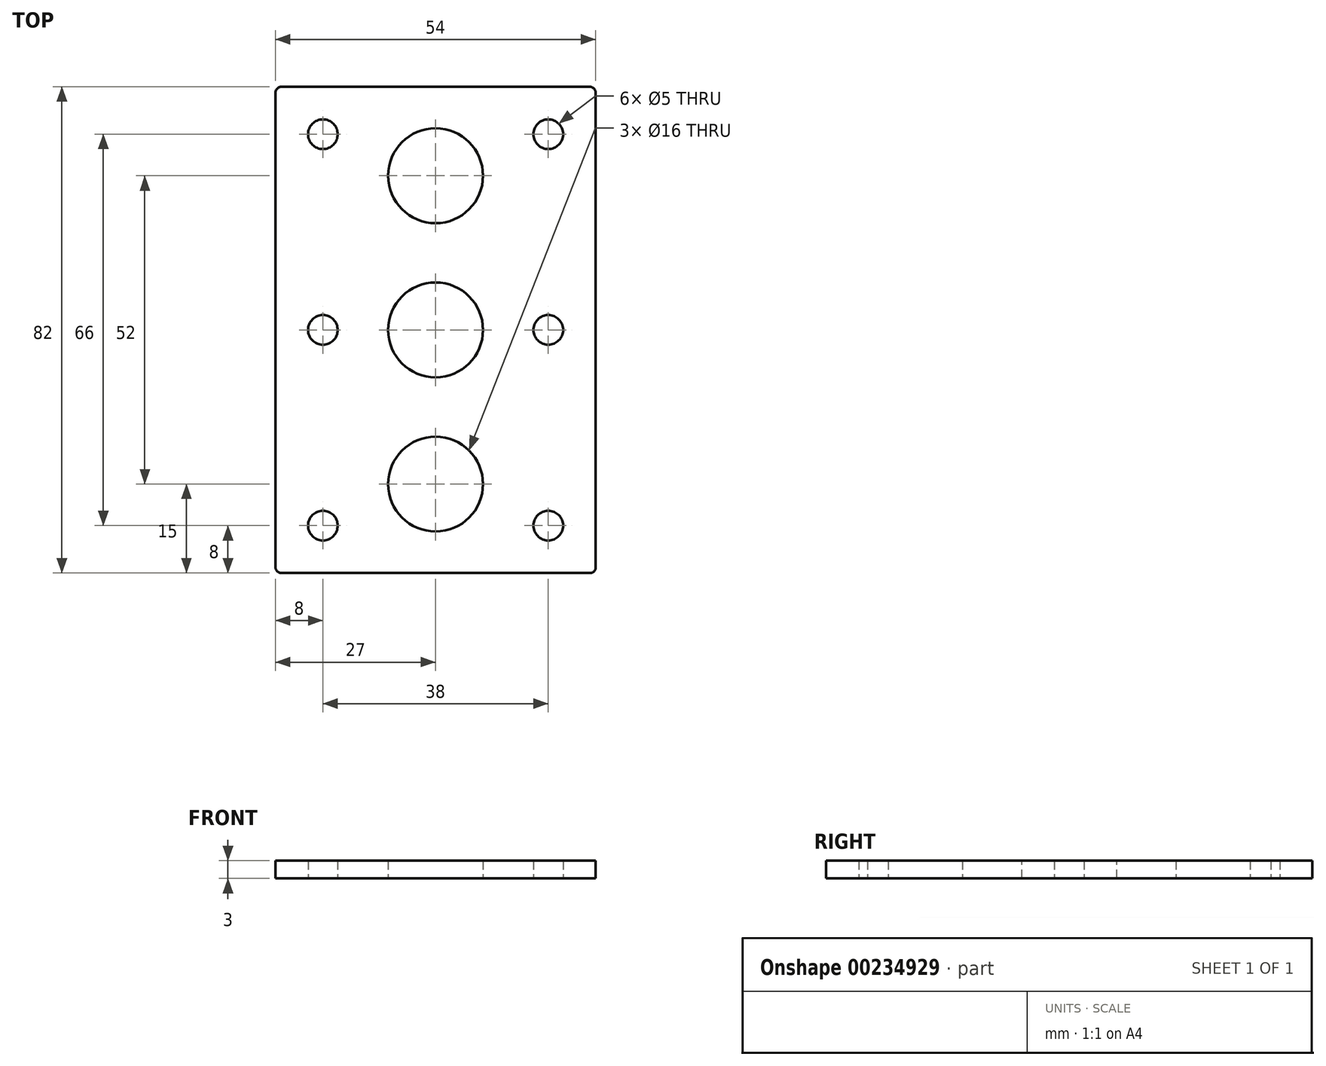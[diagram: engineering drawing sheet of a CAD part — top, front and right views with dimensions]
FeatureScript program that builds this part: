
annotation { "Feature Type Name" : "Feature", "Feature Type Description" : "" }
export const myFeature = defineFeature(function(context is Context, id is Id, definition is map)
    precondition{}
    {
        {
            var Q0;
            Q0=qCreatedBy(makeId("Top.planeOp"),FACE);
            var sketch = newSketch(context, id + "F0", { "sketchPlane" : qUnion([Q0])});
            skLineSegment(sketch, "E0.bottom", {"start": v(27, 41) * mm, "end": v(-27, 41) * mm});
            skLineSegment(sketch, "E0.top", {"start": v(27, -41) * mm, "end": v(-27, -41) * mm});
            skLineSegment(sketch, "E0.left", {"start": v(27, 41) * mm, "end": v(27, -41) * mm});
            skLineSegment(sketch, "E0.right", {"start": v(-27, 41) * mm, "end": v(-27, -41) * mm});
            skPoint(sketch, "E0.middle", {"position": v(0, 0) * mm});
            skLineSegment(sketch, "E1", {"start": v(0, -41) * mm, "end": v(0, 41) * mm, "construction": true});
            skCircle(sketch, "E2", {"center": v(0, -26) * mm, "radius": 8 * mm});
            skCircle(sketch, "E3", {"center": v(0, 26) * mm, "radius": 8 * mm});
            skLineSegment(sketch, "E4", {"start": v(-19, 41) * mm, "end": v(-19, -41) * mm, "construction": true});
            skLineSegment(sketch, "E5", {"start": v(0, 0) * mm, "end": v(-27, 0) * mm, "construction": true});
            skCircle(sketch, "E6", {"center": v(-19, 0) * mm, "radius": 2.5 * mm});
            skCircle(sketch, "E7", {"center": v(-19, -33) * mm, "radius": 2.5 * mm});
            skCircle(sketch, "E8", {"center": v(-19, 33) * mm, "radius": 2.5 * mm});
            skCircle(sketch, "E9.MirrorC", {"center": v(19, 33) * mm, "radius": 2.5 * mm});
            skCircle(sketch, "E10.MirrorC", {"center": v(19, 0) * mm, "radius": 2.5 * mm});
            skCircle(sketch, "E11.MirrorC", {"center": v(19, -33) * mm, "radius": 2.5 * mm});
            skSolve(sketch);
        }
        {
            var Q0;
            Q0 = qSketchRegion(id + "F0", true);
            extrude(context, id + "F1", {"entities" : qUnion([Q0]), "depth" : 5 * mm, "offsetDistance" : 25 * mm});
        }
        {
            var Q0;
            Q0=makeQuery(id+"F1.opExtrude","SWEPT_EDGE",EDGE,{"disambiguationData":[OSD([sQuery(id+"F0.wireOp",EDGE,"E0.top"),sQuery(id+"F0.wireOp",EDGE,"E0.left")])]});
            var Q1;
            Q1=makeQuery(id+"F1.opExtrude","SWEPT_EDGE",EDGE,{"disambiguationData":[OSD([sQuery(id+"F0.wireOp",EDGE,"E0.top"),sQuery(id+"F0.wireOp",EDGE,"E0.right")])]});
            var Q2;
            Q2=makeQuery(id+"F1.opExtrude","SWEPT_EDGE",EDGE,{"disambiguationData":[OSD([sQuery(id+"F0.wireOp",EDGE,"E0.bottom"),sQuery(id+"F0.wireOp",EDGE,"E0.right")])]});
            var Q3;
            Q3=makeQuery(id+"F1.opExtrude","SWEPT_EDGE",EDGE,{"disambiguationData":[OSD([sQuery(id+"F0.wireOp",EDGE,"E0.bottom"),sQuery(id+"F0.wireOp",EDGE,"E0.left")])]});
            fillet(context, id + "F2", {"entities" : qUnion([Q0, Q1, Q2, Q3]), "tangentPropagation" : true, "radius" : 1 * mm, "defaultsChanged" : true, "vertexSettings" : [], "allowEdgeOverflow" : false});
        }
        {
            var Q0;
            Q0=makeQuery(id+"F1.opExtrude","CAP_FACE",FACE,{"disambiguationData":[OSD([sQuery(id+"F0.wireOp",EDGE,"E0.bottom"),sQuery(id+"F0.wireOp",EDGE,"E0.top"),sQuery(id+"F0.wireOp",EDGE,"E0.left"),sQuery(id+"F0.wireOp",EDGE,"E0.right"),sQuery(id+"F0.wireOp",EDGE,"E2"),sQuery(id+"F0.wireOp",EDGE,"E3"),sQuery(id+"F0.wireOp",EDGE,"E6"),sQuery(id+"F0.wireOp",EDGE,"E7"),sQuery(id+"F0.wireOp",EDGE,"E8"),sQuery(id+"F0.wireOp",EDGE,"E9.MirrorC"),sQuery(id+"F0.wireOp",EDGE,"E10.MirrorC"),sQuery(id+"F0.wireOp",EDGE,"E11.MirrorC")])],"isStart":false});
            var sketch = newSketch(context, id + "F3", { "sketchPlane" : qUnion([Q0])});
            skCircle(sketch, "E12", {"center": v(0, 0) * mm, "radius": 8 * mm});
            skSolve(sketch);
        }
        {
            var Q0;
            Q0 = qSketchRegion(id + "F3", true);
            extrude(context, id + "F4", {"entities" : qUnion([Q0]), "operationType" : NewBodyOperationType.REMOVE, "oppositeDirection" : true, "depth" : 25 * mm, "offsetDistance" : 25 * mm});
        }
        {
            var Q0;
            Q0=makeQuery(id+"F1.opExtrude","CAP_FACE",FACE,{"disambiguationData":[OSD([sQuery(id+"F0.wireOp",EDGE,"E0.bottom"),sQuery(id+"F0.wireOp",EDGE,"E0.top"),sQuery(id+"F0.wireOp",EDGE,"E0.left"),sQuery(id+"F0.wireOp",EDGE,"E0.right"),sQuery(id+"F0.wireOp",EDGE,"E2"),sQuery(id+"F0.wireOp",EDGE,"E3"),sQuery(id+"F0.wireOp",EDGE,"E6"),sQuery(id+"F0.wireOp",EDGE,"E7"),sQuery(id+"F0.wireOp",EDGE,"E8"),sQuery(id+"F0.wireOp",EDGE,"E9.MirrorC"),sQuery(id+"F0.wireOp",EDGE,"E10.MirrorC"),sQuery(id+"F0.wireOp",EDGE,"E11.MirrorC")])],"isStart":false});
            extrude(context, id + "F5", {"entities" : qUnion([Q0]), "operationType" : NewBodyOperationType.REMOVE, "oppositeDirection" : true, "depth" : 2 * mm, "offsetDistance" : 25 * mm});
        }
    });
